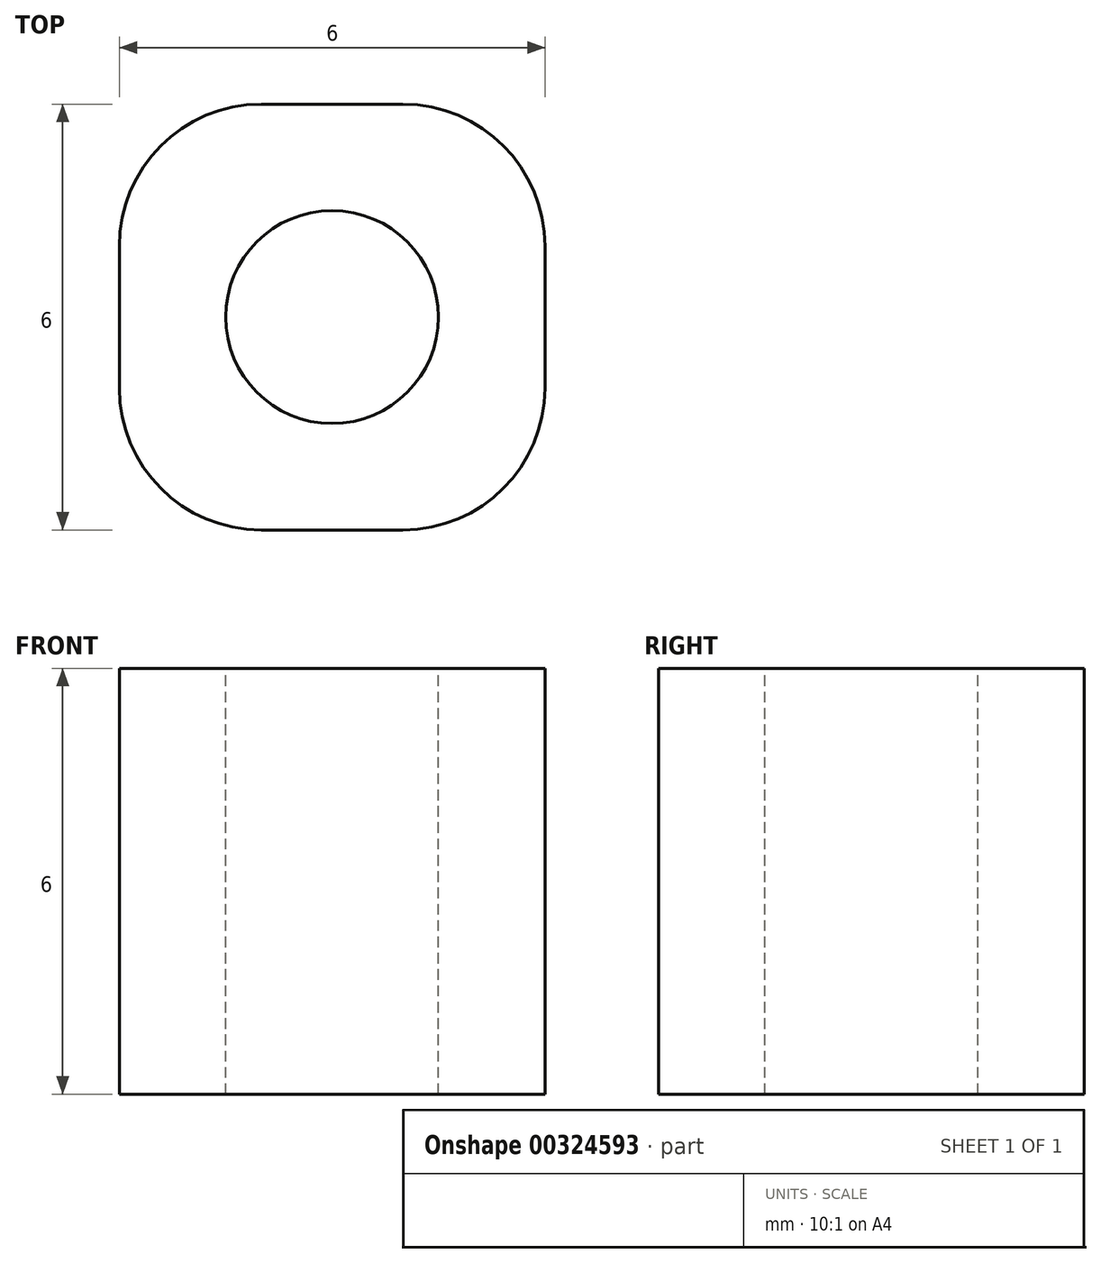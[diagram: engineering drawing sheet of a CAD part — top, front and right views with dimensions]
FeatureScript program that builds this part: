
annotation { "Feature Type Name" : "Feature", "Feature Type Description" : "" }
export const myFeature = defineFeature(function(context is Context, id is Id, definition is map)
    precondition{}
    {
        {
            var Q0;
            Q0=qCreatedBy(makeId("Top.planeOp"),FACE);
            var sketch = newSketch(context, id + "F0", { "sketchPlane" : qUnion([Q0])});
            skLineSegment(sketch, "E0.bottom", {"start": v(-23.8, 0) * mm, "end": v(-29.8, 0) * mm});
            skLineSegment(sketch, "E0.top", {"start": v(-23.8, 6) * mm, "end": v(-29.8, 6) * mm});
            skLineSegment(sketch, "E0.left", {"start": v(-23.8, 0) * mm, "end": v(-23.8, 6) * mm});
            skLineSegment(sketch, "E0.right", {"start": v(-29.8, 0) * mm, "end": v(-29.8, 6) * mm});
            skSolve(sketch);
        }
        {
            var Q0;
            Q0 = qSketchRegion(id + "F0", true);
            extrude(context, id + "F1", {"entities" : qUnion([Q0]), "depth" : 6 * mm});
        }
        {
            var Q0;
            Q0=makeQuery(id+"F1.opExtrude","SWEPT_EDGE",EDGE,{"disambiguationData":[OSD([sQuery(id+"F0.wireOp",EDGE,"E0.bottom"),sQuery(id+"F0.wireOp",EDGE,"E0.left")])]});
            var Q1;
            Q1=makeQuery(id+"F1.opExtrude","SWEPT_EDGE",EDGE,{"disambiguationData":[OSD([sQuery(id+"F0.wireOp",EDGE,"E0.bottom"),sQuery(id+"F0.wireOp",EDGE,"E0.right")])]});
            var Q2;
            Q2=makeQuery(id+"F1.opExtrude","SWEPT_EDGE",EDGE,{"disambiguationData":[OSD([sQuery(id+"F0.wireOp",EDGE,"E0.top"),sQuery(id+"F0.wireOp",EDGE,"E0.left")])]});
            var Q3;
            Q3=makeQuery(id+"F1.opExtrude","SWEPT_EDGE",EDGE,{"disambiguationData":[OSD([sQuery(id+"F0.wireOp",EDGE,"E0.top"),sQuery(id+"F0.wireOp",EDGE,"E0.right")])]});
            fillet(context, id + "F2", {"entities" : qUnion([Q0, Q1, Q2, Q3]), "radius" : 2 * mm, "tangentPropagation" : true, "allowEdgeOverflow" : false});
        }
        {
            var Q0;
            Q0=makeQuery(id+"F1.opExtrude","CAP_FACE",FACE,{"disambiguationData":[OSD([sQuery(id+"F0.wireOp",EDGE,"E0.bottom"),sQuery(id+"F0.wireOp",EDGE,"E0.top"),sQuery(id+"F0.wireOp",EDGE,"E0.left"),sQuery(id+"F0.wireOp",EDGE,"E0.right")])],"isStart":false});
            var sketch = newSketch(context, id + "F3", { "sketchPlane" : qUnion([Q0])});
            skCircle(sketch, "E1", {"center": v(-26.8, 3) * mm, "radius": 1.5 * mm});
            skPoint(sketch, "E1.centerSnap0", {"position": v(-26.8, 6) * mm});
            skPoint(sketch, "E1.centerSnap1", {"position": v(-29.8, 3) * mm});
            skSolve(sketch);
        }
        {
            var Q0;
            Q0 = qSketchRegion(id + "F3", true);
            extrude(context, id + "F4", {"entities" : qUnion([Q0]), "operationType" : NewBodyOperationType.REMOVE, "oppositeDirection" : true, "depth" : 25 * mm});
        }
    });
